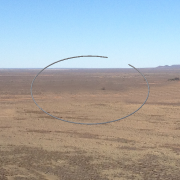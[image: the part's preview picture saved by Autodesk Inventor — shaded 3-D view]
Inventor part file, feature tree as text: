
AUTODESK INVENTOR PART (.ipt)
format: ipt  version: 2014 SP1 (Build 180222100, 222)  size: 164,352 bytes
history: native  units: in
note: dims shown in document units (in); Inventor stores cm internally (conversion verified against a paired STEP export)
features: sketch x2, sweep x1
ambient origin geometry x8: Origin, YZ Plane, XZ Plane, XY Plane, X Axis, Y Axis, Z Axis, Center Point
bodies: Solid1 (feature_tree)
feature tree (3):
  sweep  "Sweep1"
  sketch  "Sketch1"  dims[d0=3.937in d1=0.175in]
  sketch  "Sketch2"  dims[d2=393.7008in d3=196.8504in d5=0.0in]
